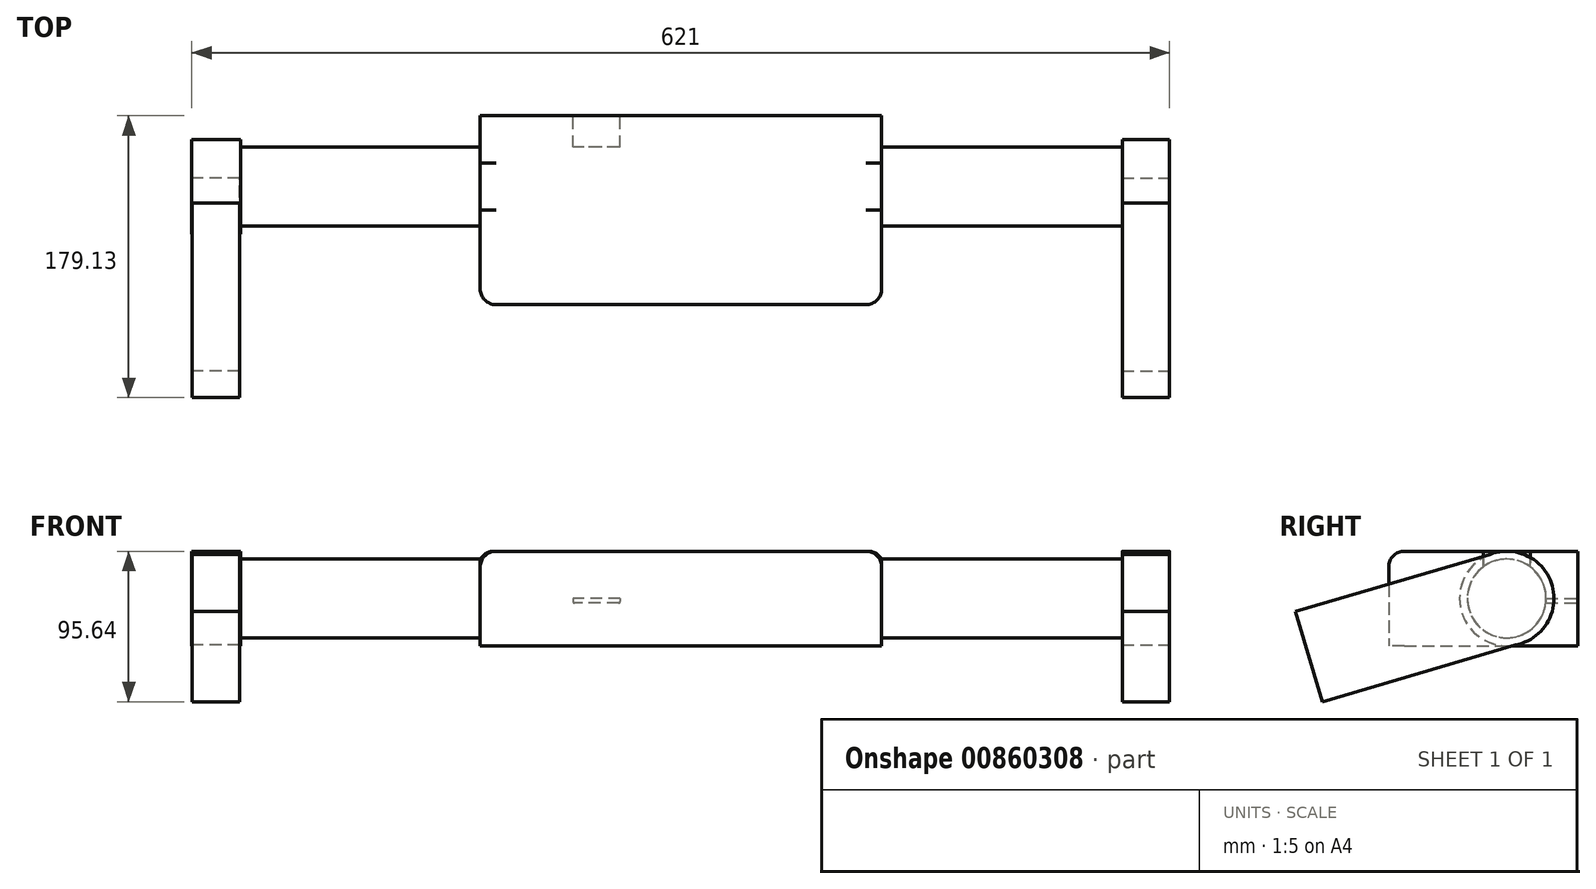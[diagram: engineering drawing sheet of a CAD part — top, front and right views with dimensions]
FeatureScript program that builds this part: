
annotation { "Feature Type Name" : "Feature", "Feature Type Description" : "" }
export const myFeature = defineFeature(function(context is Context, id is Id, definition is map)
    precondition{}
    {
        {
            var Q0;
            Q0=qCreatedBy(makeId("Front.planeOp"),FACE);
            var sketch = newSketch(context, id + "F0", { "sketchPlane" : qUnion([Q0])});
            skLineSegment(sketch, "E0", {"start": v(-289.66, 0) * mm, "end": v(310.34, 0) * mm});
            skSolve(sketch);
        }
        {
            var Q0;
            Q0=qCreatedBy(makeId("Right.planeOp"),FACE);
            var sketch = newSketch(context, id + "F1", { "sketchPlane" : qUnion([Q0])});
            skCircle(sketch, "E1", {"center": v(0, 0) * mm, "radius": 25 * mm});
            skSolve(sketch);
        }
        {
            var Q0;
            Q0=qCreatedBy(makeId("Top.planeOp"),FACE);
            var sketch = newSketch(context, id + "F2", { "sketchPlane" : qUnion([Q0])});
            skLineSegment(sketch, "E2.bottom", {"start": v(-127.5, -75) * mm, "end": v(127.5, -75) * mm});
            skLineSegment(sketch, "E2.top", {"start": v(-127.5, 45) * mm, "end": v(127.5, 45) * mm});
            skLineSegment(sketch, "E2.left", {"start": v(-127.5, -75) * mm, "end": v(-127.5, 45) * mm});
            skLineSegment(sketch, "E2.right", {"start": v(127.5, -75) * mm, "end": v(127.5, 45) * mm});
            skSolve(sketch);
        }
        {
            var Q0;
            Q0=makeQuery(id+"F1.imprint","IMPRINT",FACE,{"disambiguationData":[TD([[makeQuery(id+"F1.imprint","IMPRINT",EDGE,{"derivedFrom":sQuery(id+"F1.wireOp",EDGE,"E1")}),1.0]])]});
            var Q1;
            Q1=sQuery(id+"F0.wireOp",EDGE,"E0");
            sweep(context, id + "F3", {"profiles" : qUnion([Q0]), "path" : qUnion([Q1])});
        }
        {
            var Q0;
            Q0=makeQuery(id+"F2.imprint","IMPRINT",FACE,{"disambiguationData":[TD([[makeQuery(id+"F2.imprint","IMPRINT",EDGE,{"derivedFrom":sQuery(id+"F2.wireOp",EDGE,"E2.bottom")}),1.0]])]});
            extrude(context, id + "F4", {"entities" : qUnion([Q0]), "operationType" : NewBodyOperationType.ADD, "endBound" : BoundingType.SYMMETRIC, "depth" : 60 * mm, "offsetDistance" : 25 * mm});
        }
        {
            var Q0;
            Q0=makeQuery(id+"F4.opExtrude","CAP_EDGE",EDGE,{"disambiguationData":[OSD([sQuery(id+"F2.wireOp",EDGE,"E2.left")])],"isStart":false});
            var Q1;
            Q1=makeQuery(id+"F4.opExtrude","CAP_EDGE",EDGE,{"disambiguationData":[OSD([sQuery(id+"F2.wireOp",EDGE,"E2.bottom")])],"isStart":false});
            var Q2;
            Q2=makeQuery(id+"F4.opExtrude","CAP_EDGE",EDGE,{"disambiguationData":[OSD([sQuery(id+"F2.wireOp",EDGE,"E2.right")])],"isStart":false});
            var Q3;
            Q3=makeQuery(id+"F4.opExtrude","SWEPT_EDGE",EDGE,{"disambiguationData":[OSD([sQuery(id+"F2.wireOp",EDGE,"E2.bottom"),sQuery(id+"F2.wireOp",EDGE,"E2.right")])]});
            var Q4;
            Q4=makeQuery(id+"F4.opExtrude","SWEPT_EDGE",EDGE,{"disambiguationData":[OSD([sQuery(id+"F2.wireOp",EDGE,"E2.bottom"),sQuery(id+"F2.wireOp",EDGE,"E2.left")])]});
            fillet(context, id + "F5", {"entities" : qUnion([Q0, Q1, Q2, Q3, Q4]), "radius" : 10 * mm, "tangentPropagation" : true, "allowEdgeOverflow" : false});
        }
        {
            var Q0;
            Q0=makeQuery(id+"F4.opExtrude","SWEPT_FACE",FACE,{"disambiguationData":[OSD([sQuery(id+"F2.wireOp",EDGE,"E2.top")])]});
            var sketch = newSketch(context, id + "F6", { "sketchPlane" : qUnion([Q0])});
            skLineSegment(sketch, "E3.bottom", {"start": v(38.57, 0) * mm, "end": v(68.57, 0) * mm});
            skLineSegment(sketch, "E3.top", {"start": v(38.57, -3) * mm, "end": v(68.57, -3) * mm});
            skLineSegment(sketch, "E3.left", {"start": v(38.57, 0) * mm, "end": v(38.57, -3) * mm});
            skLineSegment(sketch, "E3.right", {"start": v(68.57, 0) * mm, "end": v(68.57, -3) * mm});
            skSolve(sketch);
        }
        {
            var Q0;
            Q0=makeQuery(id+"F6.imprint","IMPRINT",FACE,{"disambiguationData":[TD([[makeQuery(id+"F6.imprint","IMPRINT",EDGE,{"derivedFrom":sQuery(id+"F6.wireOp",EDGE,"E3.bottom")}),-1.0]])]});
            extrude(context, id + "F7", {"entities" : qUnion([Q0]), "operationType" : NewBodyOperationType.REMOVE, "oppositeDirection" : true, "depth" : 20 * mm, "offsetDistance" : 25 * mm});
        }
        {
            var Q0;
            Q0=makeQuery(id+"F7.boolean.opBoolean","COPY",EDGE,{"derivedFrom":makeQuery(id+"F7.opExtrude","CAP_EDGE",EDGE,{"disambiguationData":[OSD([sQuery(id+"F6.wireOp",EDGE,"E3.bottom")])],"isStart":true})});
            var Q1;
            Q1=makeQuery(id+"F7.boolean.opBoolean","COPY",EDGE,{"derivedFrom":makeQuery(id+"F7.opExtrude","CAP_EDGE",EDGE,{"disambiguationData":[OSD([sQuery(id+"F6.wireOp",EDGE,"E3.left")])],"isStart":true})});
            var Q2;
            Q2=makeQuery(id+"F7.boolean.opBoolean","COPY",EDGE,{"derivedFrom":makeQuery(id+"F7.opExtrude","CAP_EDGE",EDGE,{"disambiguationData":[OSD([sQuery(id+"F6.wireOp",EDGE,"E3.right")])],"isStart":true})});
            var Q3;
            Q3=makeQuery(id+"F7.boolean.opBoolean","COPY",EDGE,{"derivedFrom":makeQuery(id+"F7.opExtrude","CAP_EDGE",EDGE,{"disambiguationData":[OSD([sQuery(id+"F6.wireOp",EDGE,"E3.top")])],"isStart":true})});
            var Q4;
            Q4=makeQuery(id+"F7.boolean.opBoolean","COPY",EDGE,{"derivedFrom":makeQuery(id+"F7.opExtrude","SWEPT_EDGE",EDGE,{"disambiguationData":[OSD([sQuery(id+"F6.wireOp",EDGE,"E3.top"),sQuery(id+"F6.wireOp",EDGE,"E3.right")])]})});
            var Q5;
            Q5=makeQuery(id+"F7.boolean.opBoolean","COPY",EDGE,{"derivedFrom":makeQuery(id+"F7.opExtrude","SWEPT_EDGE",EDGE,{"disambiguationData":[OSD([sQuery(id+"F6.wireOp",EDGE,"E3.top"),sQuery(id+"F6.wireOp",EDGE,"E3.left")])]})});
            fillet(context, id + "F8", {"entities" : qUnion([Q0, Q1, Q2, Q3, Q4, Q5]), "radius" : 1 * mm, "tangentPropagation" : true, "allowEdgeOverflow" : false});
        }
        {
            var Q0;
            Q0=makeQuery(id+"F3.opSweep","CAP_FACE",FACE,{"disambiguationData":[OSD([sQuery(id+"F0.wireOp",VERTEX,"E0.end"),sQuery(id+"F1.wireOp",EDGE,"E1")])],"isStart":false});
            var sketch = newSketch(context, id + "F9", { "sketchPlane" : qUnion([Q0])});
            skCircle(sketch, "E4", {"center": v(0, 0) * mm, "radius": 30 * mm});
            skSolve(sketch);
        }
        {
            var Q0;
            Q0=makeQuery(id+"F9.imprint","IMPRINT",FACE,{"disambiguationData":[TD([[makeQuery(id+"F9.imprint","IMPRINT",EDGE,{"derivedFrom":sQuery(id+"F9.wireOp",EDGE,"E4")}),1.0]])]});
            extrude(context, id + "F10", {"entities" : qUnion([Q0]), "operationType" : NewBodyOperationType.ADD, "oppositeDirection" : true, "depth" : 30 * mm, "offsetDistance" : 25 * mm});
        }
        {
            var Q0;
            {var subQ0=sQuery(id+"F1.wireOp",EDGE,"E1");var subQ1=sQuery(id+"F0.wireOp",VERTEX,"E0.end");Q0=makeQuery(id+"F10.boolean.opBoolean","MERGE",FACE,{"derivedFrom":[makeQuery(id+"F3.opSweep","CAP_FACE",FACE,{"disambiguationData":[OSD([subQ1,subQ0])],"isStart":false}),makeQuery(id+"F10.opExtrude","CAP_FACE",FACE,{"disambiguationData":[OSD([subQ1,subQ0,sQuery(id+"F9.wireOp",EDGE,"E4")])],"isStart":true})]});}
            var sketch = newSketch(context, id + "F11", { "sketchPlane" : qUnion([Q0])});
            skLineSegment(sketch, "E5", {"start": v(-6.38, 29.31) * mm, "end": v(-134.13, -8.32) * mm});
            skLineSegment(sketch, "E6", {"start": v(5.43, -29.5) * mm, "end": v(-117.24, -65.64) * mm});
            skLineSegment(sketch, "E7", {"start": v(-117.24, -65.64) * mm, "end": v(-134.13, -8.32) * mm});
            skPoint(sketch, "E8.orphan", {"position": v(-133.79, -9.48) * mm});
            skPoint(sketch, "E9.orphan", {"position": v(-138.07, -9.48) * mm});
            skSolve(sketch);
        }
        {
            var Q0;
            {var subQ4=sQuery(id+"F11.wireOp",EDGE,"E6");Q0=makeQuery(id+"F11.imprint","IMPRINT",FACE,{"disambiguationData":[TD([[makeQuery(id+"F11.imprint","IMPRINT",EDGE,{"derivedFrom":subQ4}),-1.0]])]});}
            extrude(context, id + "F12", {"entities" : qUnion([Q0]), "oppositeDirection" : true, "depth" : 30 * mm, "offsetDistance" : 25 * mm});
        }
        {
            var Q0;
            Q0=makeQuery(id+"F3.opSweep","CAP_FACE",FACE,{"disambiguationData":[OSD([sQuery(id+"F0.wireOp",VERTEX,"E0.start"),sQuery(id+"F1.wireOp",EDGE,"E1")])],"isStart":true});
            var sketch = newSketch(context, id + "F13", { "sketchPlane" : qUnion([Q0])});
            skCircle(sketch, "E10", {"center": v(0, 0) * mm, "radius": 30 * mm});
            skSolve(sketch);
        }
        {
            var Q0;
            Q0=qSketchRegion(id+"F13",true);
            extrude(context, id + "F14", {"entities" : qUnion([Q0]), "operationType" : NewBodyOperationType.ADD, "oppositeDirection" : true, "depth" : 10 * mm, "offsetDistance" : 25 * mm});
        }
        {
            var Q0;
            Q0=makeQuery(id+"F12.opExtrude","SWEPT_BODY",BODY,{"disambiguationData":[OSD([sQuery(id+"F9.wireOp",EDGE,"E4"),sQuery(id+"F11.wireOp",EDGE,"E5"),sQuery(id+"F11.wireOp",EDGE,"E6"),sQuery(id+"F11.wireOp",EDGE,"E7")])]});
            var Q1;
            Q1=qCreatedBy(makeId("Right.planeOp"),FACE);
            mirror(context, id + "F15", {"operationType" : NewBodyOperationType.ADD, "entities" : qUnion([Q0]), "mirrorPlane" : qUnion([Q1])});
        }
        {
            var Q0;
            Q0=makeQuery(id+"F14.boolean.opBoolean","MERGE",FACE,{"derivedFrom":[makeQuery(id+"F3.opSweep","CAP_FACE",FACE,{"disambiguationData":[OSD([sQuery(id+"F0.wireOp",VERTEX,"E0.start"),sQuery(id+"F1.wireOp",EDGE,"E1")])],"isStart":true}),makeQuery(id+"F14.opExtrude","CAP_FACE",FACE,{"disambiguationData":[OSD([sQuery(id+"F13.wireOp",EDGE,"E10")])],"isStart":true})]});
            extrude(context, id + "F16", {"entities" : qUnion([Q0]), "operationType" : NewBodyOperationType.ADD, "depth" : 21 * mm, "offsetDistance" : 25 * mm});
        }
    });
